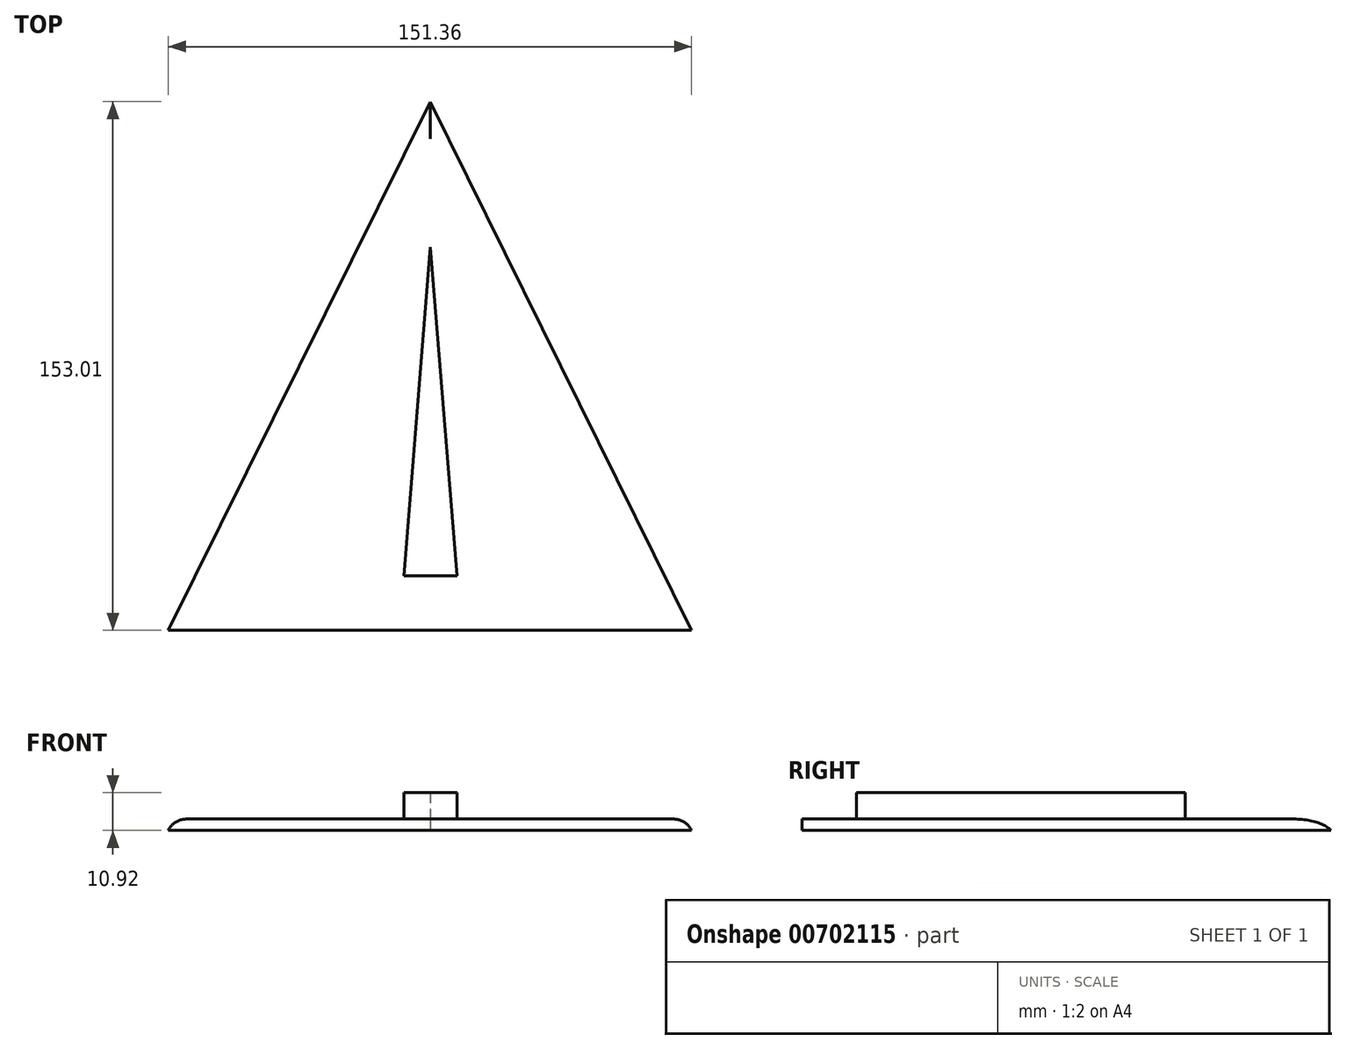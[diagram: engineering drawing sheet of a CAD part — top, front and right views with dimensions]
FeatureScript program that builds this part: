
annotation { "Feature Type Name" : "Feature", "Feature Type Description" : "" }
export const myFeature = defineFeature(function(context is Context, id is Id, definition is map)
    precondition{}
    {
        {
            var Q0;
            Q0=qCreatedBy(makeId("Top.planeOp"),FACE);
            var sketch = newSketch(context, id + "F0", { "sketchPlane" : qUnion([Q0])});
            skLineSegment(sketch, "E0", {"start": v(0, 77.02) * mm, "end": v(-75.78, -76) * mm});
            skLineSegment(sketch, "E1", {"start": v(-75.78, -76) * mm, "end": v(75.58, -76) * mm});
            skLineSegment(sketch, "E2", {"start": v(75.58, -76) * mm, "end": v(0, 77.02) * mm});
            skSolve(sketch);
        }
        {
            var Q0;
            Q0 = qSketchRegion(id + "F0", true);
            extrude(context, id + "F1", {"entities" : qUnion([Q0]), "depth" : 3.3 * mm, "offsetDistance" : 25.4 * mm});
        }
        {
            var Q0;
            Q0=makeQuery(id+"F1.opExtrude","CAP_EDGE",EDGE,{"disambiguationData":[OSD([sQuery(id+"F0.wireOp",EDGE,"E0")])],"isStart":false});
            var Q1;
            Q1=makeQuery(id+"F1.opExtrude","CAP_EDGE",EDGE,{"disambiguationData":[OSD([sQuery(id+"F0.wireOp",EDGE,"E2")])],"isStart":false});
            fillet(context, id + "F2", {"entities" : qUnion([Q0, Q1]), "radius" : 5.08 * mm, "tangentPropagation" : true, "allowEdgeOverflow" : false});
        }
        {
            var Q0;
            Q0=makeQuery(id+"F1.opExtrude","CAP_FACE",FACE,{"disambiguationData":[OSD([sQuery(id+"F0.wireOp",EDGE,"E0"),sQuery(id+"F0.wireOp",EDGE,"E1"),sQuery(id+"F0.wireOp",EDGE,"E2")])],"isStart":false});
            var sketch = newSketch(context, id + "F3", { "sketchPlane" : qUnion([Q0])});
            skLineSegment(sketch, "E3", {"start": v(0, 34.93) * mm, "end": v(-7.57, -60.23) * mm});
            skLineSegment(sketch, "E4", {"start": v(-7.57, -60.23) * mm, "end": v(7.77, -60.23) * mm});
            skLineSegment(sketch, "E5", {"start": v(7.77, -60.23) * mm, "end": v(0, 34.93) * mm});
            skSolve(sketch);
        }
        {
            var Q0;
            Q0 = qSketchRegion(id + "F3", true);
            extrude(context, id + "F4", {"entities" : qUnion([Q0]), "operationType" : NewBodyOperationType.ADD, "depth" : 7.62 * mm, "offsetDistance" : 25.4 * mm});
        }
    });
